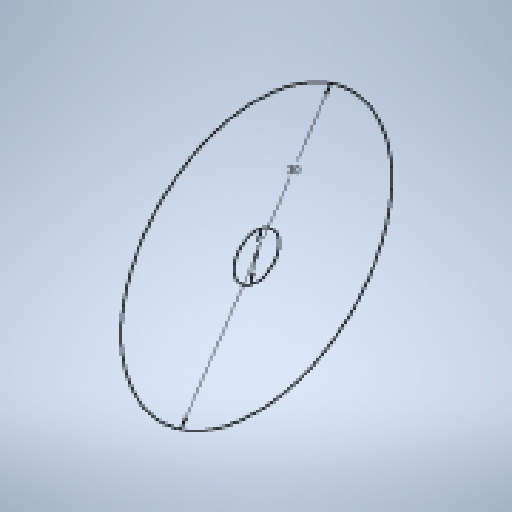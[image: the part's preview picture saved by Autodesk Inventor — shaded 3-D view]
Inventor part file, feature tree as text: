
AUTODESK INVENTOR PART (.ipt)
format: ipt  version: 2023 (Build 270158000, 158)  size: 176,640 bytes
history: native  units: mm
features: extrude x4, sketch x4, other x1
ambient origin geometry x8: Origin, YZ Plane, XZ Plane, XY Plane, X Axis, Y Axis, Z Axis, Center Point
bodies: Body1 (feature_tree)
feature tree (9):
  other  "實體1"
  extrude  "擠出1"  Depth=5.0mm
  extrude  "擠出2"  Depth=30.0mm
  extrude  "擠出3"  Depth=3.0mm TaperAngle=0.0deg
  extrude  "擠出4"  Depth=18.5mm
  sketch  "草圖1"
  sketch  "草圖2"
  sketch  "草圖3"
  sketch  "草圖4"
